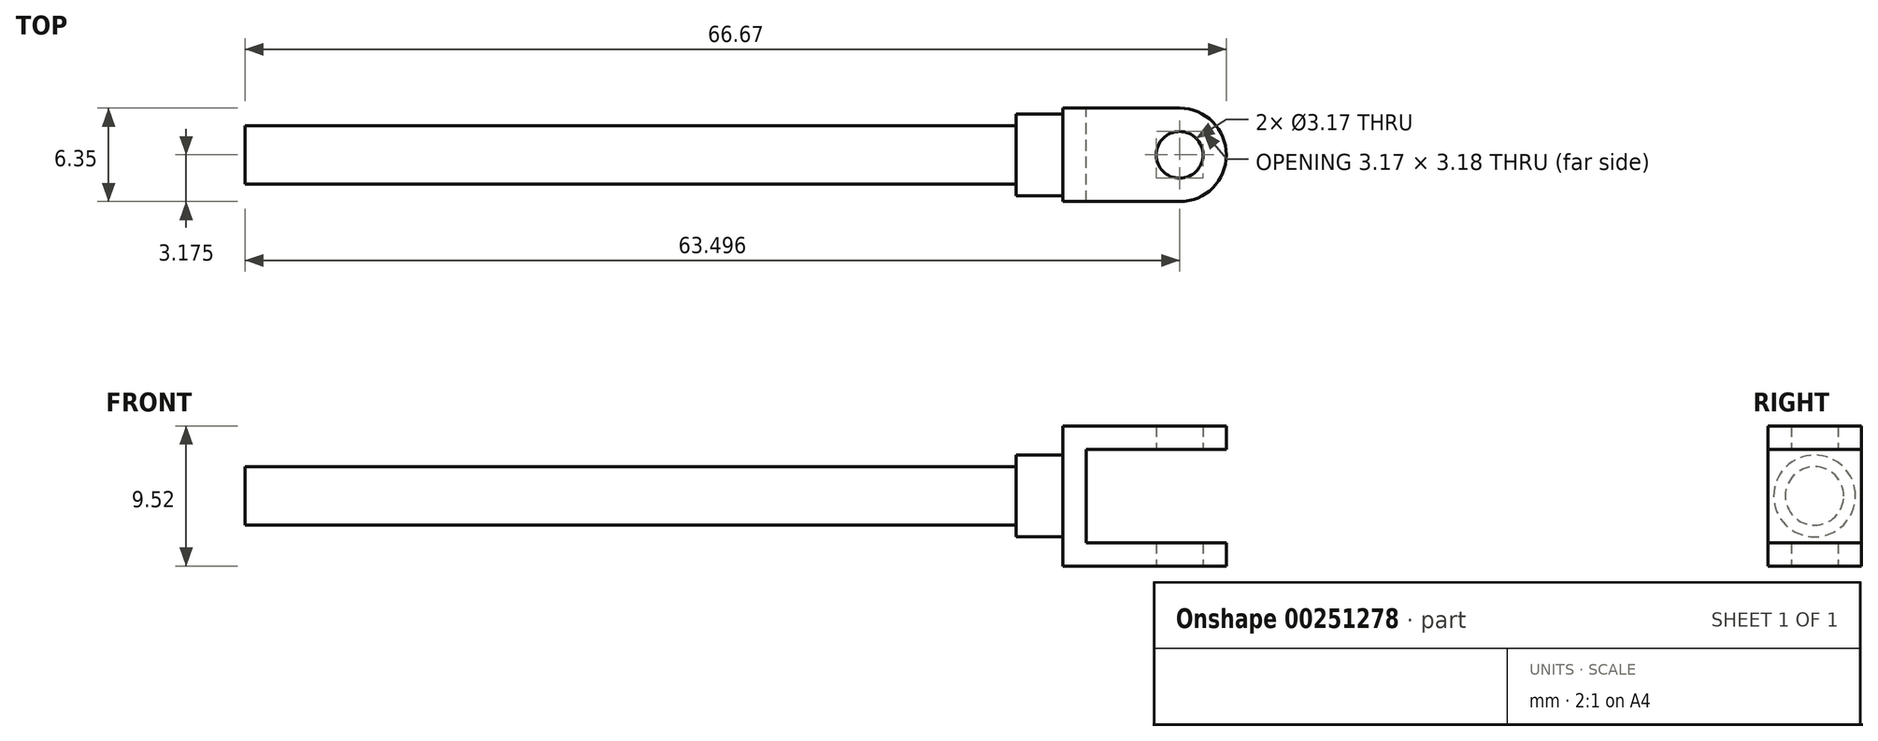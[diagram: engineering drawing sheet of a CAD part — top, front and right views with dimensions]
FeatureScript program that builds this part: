
annotation { "Feature Type Name" : "Feature", "Feature Type Description" : "" }
export const myFeature = defineFeature(function(context is Context, id is Id, definition is map)
    precondition{}
    {
        {
            var Q0;
            Q0=qCreatedBy(makeId("Front.planeOp"),FACE);
            var sketch = newSketch(context, id + "F0", { "sketchPlane" : qUnion([Q0])});
            skLineSegment(sketch, "E0", {"start": v(33.25, 28.06) * mm, "end": v(22.14, 28.06) * mm});
            skLineSegment(sketch, "E1", {"start": v(22.14, 28.06) * mm, "end": v(22.14, 18.54) * mm});
            skLineSegment(sketch, "E2", {"start": v(22.14, 18.54) * mm, "end": v(33.25, 18.54) * mm});
            skLineSegment(sketch, "E3", {"start": v(33.25, 18.54) * mm, "end": v(33.25, 20.12) * mm});
            skLineSegment(sketch, "E4", {"start": v(33.25, 20.12) * mm, "end": v(23.73, 20.12) * mm});
            skLineSegment(sketch, "E5", {"start": v(23.73, 20.12) * mm, "end": v(23.73, 26.47) * mm});
            skLineSegment(sketch, "E6", {"start": v(23.73, 26.47) * mm, "end": v(33.25, 26.47) * mm});
            skLineSegment(sketch, "E7", {"start": v(33.25, 26.47) * mm, "end": v(33.25, 28.06) * mm});
            skSolve(sketch);
        }
        {
            var Q0;
            Q0 = qSketchRegion(id + "F0", true);
            extrude(context, id + "F1", {"entities" : qUnion([Q0]), "depth" : 6.35 * mm});
        }
        {
            var Q0;
            Q0=makeQuery(id+"F1.opExtrude","CAP_EDGE",EDGE,{"disambiguationData":[OSD([sQuery(id+"F0.wireOp",EDGE,"E3")])],"isStart":false});
            var Q1;
            Q1=makeQuery(id+"F1.opExtrude","CAP_EDGE",EDGE,{"disambiguationData":[OSD([sQuery(id+"F0.wireOp",EDGE,"E7")])],"isStart":false});
            var Q2;
            Q2=makeQuery(id+"F1.opExtrude","CAP_EDGE",EDGE,{"disambiguationData":[OSD([sQuery(id+"F0.wireOp",EDGE,"E7")])],"isStart":true});
            var Q3;
            Q3=makeQuery(id+"F1.opExtrude","CAP_EDGE",EDGE,{"disambiguationData":[OSD([sQuery(id+"F0.wireOp",EDGE,"E3")])],"isStart":true});
            fillet(context, id + "F2", {"entities" : qUnion([Q0, Q1, Q2, Q3]), "radius" : 3.17 * mm, "tangentPropagation" : true, "allowEdgeOverflow" : false});
        }
        {
            var Q0;
            Q0=makeQuery(id+"F1.opExtrude","SWEPT_FACE",FACE,{"disambiguationData":[OSD([sQuery(id+"F0.wireOp",EDGE,"E0")])]});
            var sketch = newSketch(context, id + "F3", { "sketchPlane" : qUnion([Q0])});
            skPoint(sketch, "E8", {"position": v(30.08, -3.18) * mm});
            skSolve(sketch);
        }
        {
            var Q0;
            Q0=sQuery(id+"F3.wireOp",VERTEX,"E8");
            var Q1;
            Q1=makeQuery(id+"F1.opExtrude","SWEPT_BODY",BODY,{"disambiguationData":[OSD([sQuery(id+"F0.wireOp",EDGE,"E0"),sQuery(id+"F0.wireOp",EDGE,"E1"),sQuery(id+"F0.wireOp",EDGE,"E2"),sQuery(id+"F0.wireOp",EDGE,"E3"),sQuery(id+"F0.wireOp",EDGE,"E4"),sQuery(id+"F0.wireOp",EDGE,"E5"),sQuery(id+"F0.wireOp",EDGE,"E6"),sQuery(id+"F0.wireOp",EDGE,"E7")])]});
            hole(context, id + "F4", {"style" : HoleStyle.SIMPLE, "endStyle" : HoleEndStyle.THROUGH, "holeDiameter" : 3.17 * mm, "tappedDepth" : 12.7 * mm, "tapClearance" : 3, "locations" : qUnion([Q0]), "scope" : qUnion([Q1]), "startStyle" : HoleStartStyle.PART});
        }
        {
            var Q0;
            Q0=makeQuery(id+"F1.opExtrude","SWEPT_FACE",FACE,{"disambiguationData":[OSD([sQuery(id+"F0.wireOp",EDGE,"E1")])]});
            var sketch = newSketch(context, id + "F5", { "sketchPlane" : qUnion([Q0])});
            skCircle(sketch, "E9", {"center": v(3.18, 23.3) * mm, "radius": 2.78 * mm});
            skSolve(sketch);
        }
        {
            var Q0;
            Q0 = qSketchRegion(id + "F5", true);
            extrude(context, id + "F6", {"entities" : qUnion([Q0]), "operationType" : NewBodyOperationType.ADD, "depth" : 3.17 * mm});
        }
        {
            var Q0;
            Q0=makeQuery(id+"F6.opExtrude","CAP_FACE",FACE,{"disambiguationData":[OSD([sQuery(id+"F5.wireOp",EDGE,"E9")])],"isStart":false});
            var sketch = newSketch(context, id + "F7", { "sketchPlane" : qUnion([Q0])});
            skCircle(sketch, "E10", {"center": v(3.18, 23.3) * mm, "radius": 1.98 * mm});
            skSolve(sketch);
        }
        {
            var Q0;
            Q0 = qSketchRegion(id + "F7", true);
            extrude(context, id + "F8", {"entities" : qUnion([Q0]), "operationType" : NewBodyOperationType.ADD, "depth" : 52.4 * mm});
        }
    });
